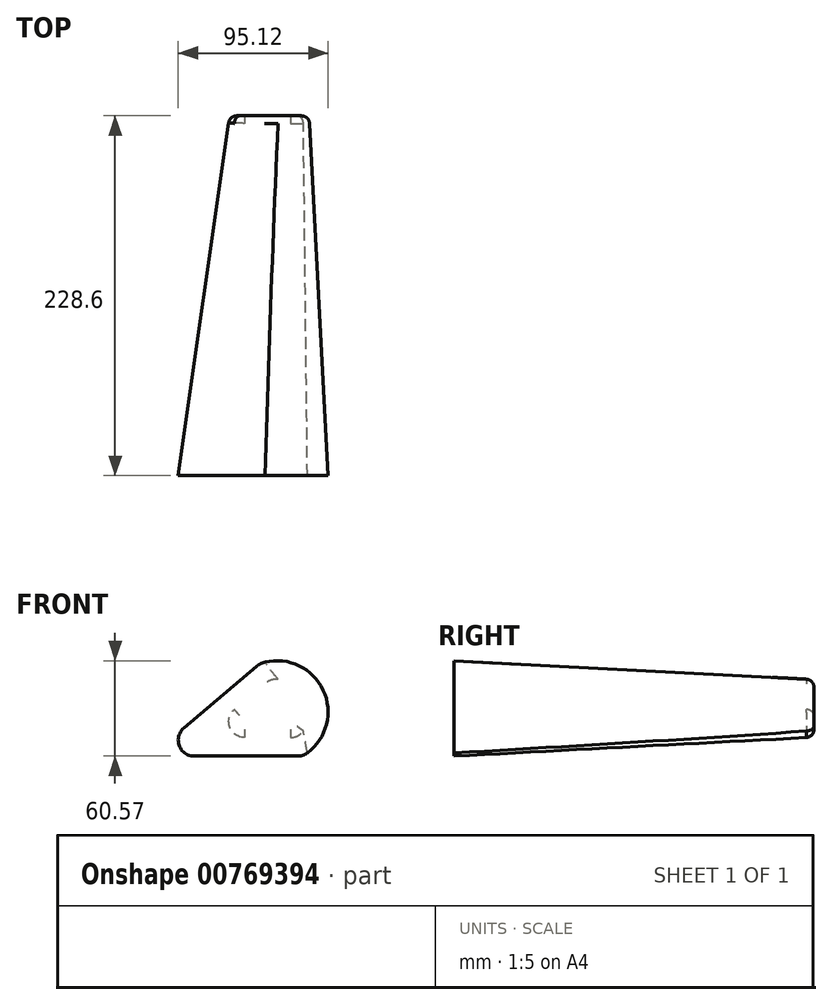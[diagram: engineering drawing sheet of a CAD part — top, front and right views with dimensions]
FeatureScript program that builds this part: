
annotation { "Feature Type Name" : "Feature", "Feature Type Description" : "" }
export const myFeature = defineFeature(function(context is Context, id is Id, definition is map)
    precondition{}
    {
        {
            var Q0;
            Q0=qCreatedBy(makeId("Front.planeOp"),FACE);
            var sketch = newSketch(context, id + "F0", { "sketchPlane" : qUnion([Q0])});
            skLineSegment(sketch, "E0", {"start": v(29.38, 0) * mm, "end": v(-30.76, 0) * mm});
            skLineSegment(sketch, "E1", {"start": v(-30.76, 0) * mm, "end": v(11.73, 36) * mm});
            skArc(sketch, "E2", {"start": v(29.38, 0) * mm, "mid": v(35.1, 25.13) * mm, "end": v(11.73, 36) * mm});
            skSolve(sketch);
        }
        {
            var Q0;
            Q0 = qSketchRegion(id + "F0", true);
            extrude(context, id + "F1", {"entities" : qUnion([Q0]), "depth" : 228.6 * mm, "offsetDistance" : 25.4 * mm, "hasDraft" : true, "draftAngle" : 3 * degree});
        }
        {
            var Q0;
            Q0=makeQuery(id+"F1.opExtrude","SWEPT_EDGE",EDGE,{"disambiguationData":[OSD([sQuery(id+"F0.wireOp",EDGE,"E1"),sQuery(id+"F0.wireOp",EDGE,"E2")])]});
            fillet(context, id + "F2", {"entities" : qUnion([Q0]), "radius" : 12.7 * mm, "tangentPropagation" : true, "allowEdgeOverflow" : false});
        }
        {
            var Q0;
            Q0=makeQuery(id+"F1.opExtrude","SWEPT_EDGE",EDGE,{"disambiguationData":[OSD([sQuery(id+"F0.wireOp",EDGE,"E0"),sQuery(id+"F0.wireOp",EDGE,"E1")])]});
            fillet(context, id + "F3", {"entities" : qUnion([Q0]), "radius" : 10.16 * mm, "tangentPropagation" : true, "allowEdgeOverflow" : false});
        }
        {
            var Q0;
            Q0=makeQuery(id+"F1.opExtrude","SWEPT_EDGE",EDGE,{"disambiguationData":[OSD([sQuery(id+"F0.wireOp",EDGE,"E0"),sQuery(id+"F0.wireOp",EDGE,"E2")])]});
            fillet(context, id + "F4", {"entities" : qUnion([Q0]), "radius" : 10.16 * mm, "tangentPropagation" : true, "allowEdgeOverflow" : false});
        }
        {
            var Q0;
            Q0=makeQuery(id+"F1.opExtrude","CAP_FACE",FACE,{"disambiguationData":[OSD([sQuery(id+"F0.wireOp",EDGE,"E0"),sQuery(id+"F0.wireOp",EDGE,"E1"),sQuery(id+"F0.wireOp",EDGE,"E2")])],"isStart":true});
            fillet(context, id + "F5", {"entities" : qUnion([Q0]), "radius" : 5.08 * mm, "tangentPropagation" : true, "allowEdgeOverflow" : false});
        }
    });
